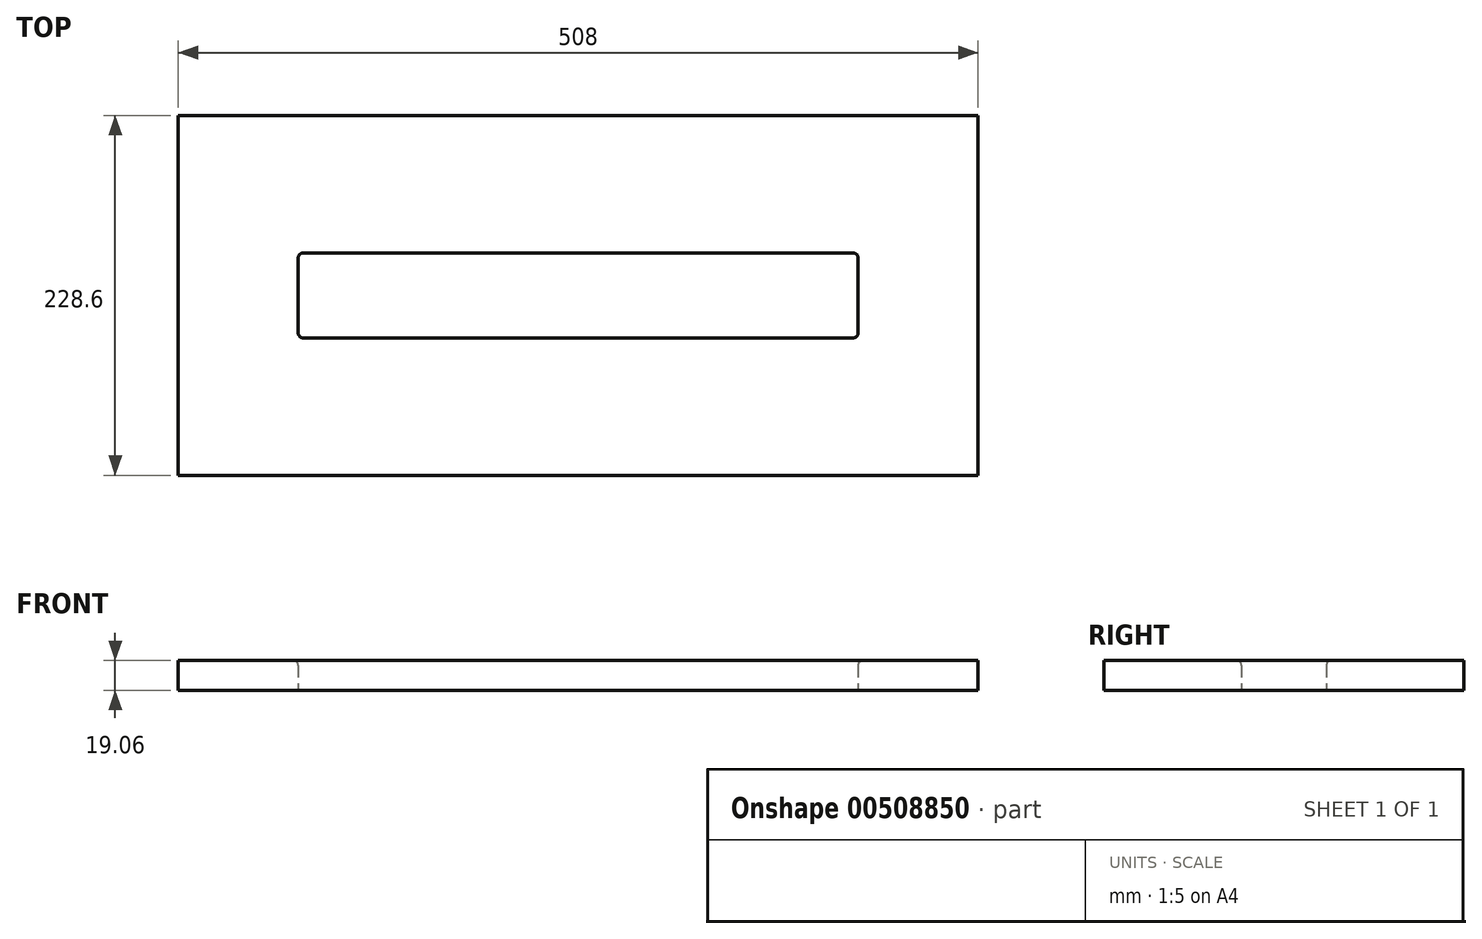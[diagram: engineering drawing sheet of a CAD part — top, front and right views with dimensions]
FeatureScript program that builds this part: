
annotation { "Feature Type Name" : "Feature", "Feature Type Description" : "" }
export const myFeature = defineFeature(function(context is Context, id is Id, definition is map)
    precondition{}
    {
        {
            var Q0;
            Q0=qCreatedBy(makeId("Top.planeOp"),FACE);
            var sketch = newSketch(context, id + "F0", { "sketchPlane" : qUnion([Q0])});
            skLineSegment(sketch, "E0.bottom", {"start": v(254, -114.3) * mm, "end": v(-254, -114.3) * mm});
            skLineSegment(sketch, "E0.top", {"start": v(254, 114.3) * mm, "end": v(-254, 114.3) * mm});
            skLineSegment(sketch, "E0.left", {"start": v(254, -114.3) * mm, "end": v(254, 114.3) * mm});
            skLineSegment(sketch, "E0.right", {"start": v(-254, -114.3) * mm, "end": v(-254, 114.3) * mm});
            skPoint(sketch, "E0.middle", {"position": v(0, 0) * mm});
            skLineSegment(sketch, "E1.bottom", {"start": v(177.8, -26.99) * mm, "end": v(-177.8, -26.99) * mm});
            skLineSegment(sketch, "E1.top", {"start": v(177.8, 26.99) * mm, "end": v(-177.8, 26.99) * mm});
            skLineSegment(sketch, "E1.left", {"start": v(177.8, -26.99) * mm, "end": v(177.8, 26.99) * mm});
            skLineSegment(sketch, "E1.right", {"start": v(-177.8, -26.99) * mm, "end": v(-177.8, 26.99) * mm});
            skSolve(sketch);
        }
        {
            var Q0;
            Q0=makeQuery(id+"F0.imprint","IMPRINT",FACE,{"disambiguationData":[TD([[makeQuery(id+"F0.imprint","IMPRINT",EDGE,{"derivedFrom":sQuery(id+"F0.wireOp",EDGE,"E0.bottom")}),-1.0]])]});
            extrude(context, id + "F1", {"entities" : qUnion([Q0]), "endBound" : BoundingType.SYMMETRIC, "depth" : 19.05 * mm});
        }
        {
            var Q0;
            Q0=makeQuery(id+"F1.opExtrude","CAP_EDGE",EDGE,{"disambiguationData":[OSD([sQuery(id+"F0.wireOp",EDGE,"E1.right")])],"isStart":false});
            var Q1;
            Q1=makeQuery(id+"F1.opExtrude","CAP_EDGE",EDGE,{"disambiguationData":[OSD([sQuery(id+"F0.wireOp",EDGE,"E1.top")])],"isStart":false});
            var Q2;
            Q2=makeQuery(id+"F1.opExtrude","CAP_EDGE",EDGE,{"disambiguationData":[OSD([sQuery(id+"F0.wireOp",EDGE,"E1.bottom")])],"isStart":false});
            var Q3;
            Q3=makeQuery(id+"F1.opExtrude","CAP_EDGE",EDGE,{"disambiguationData":[OSD([sQuery(id+"F0.wireOp",EDGE,"E1.left")])],"isStart":false});
            var Q4;
            Q4=makeQuery(id+"F1.opExtrude","SWEPT_EDGE",EDGE,{"disambiguationData":[OSD([sQuery(id+"F0.wireOp",EDGE,"E1.top"),sQuery(id+"F0.wireOp",EDGE,"E1.left")])]});
            var Q5;
            Q5=makeQuery(id+"F1.opExtrude","SWEPT_EDGE",EDGE,{"disambiguationData":[OSD([sQuery(id+"F0.wireOp",EDGE,"E1.top"),sQuery(id+"F0.wireOp",EDGE,"E1.right")])]});
            var Q6;
            Q6=makeQuery(id+"F1.opExtrude","SWEPT_EDGE",EDGE,{"disambiguationData":[OSD([sQuery(id+"F0.wireOp",EDGE,"E1.bottom"),sQuery(id+"F0.wireOp",EDGE,"E1.right")])]});
            var Q7;
            Q7=makeQuery(id+"F1.opExtrude","SWEPT_EDGE",EDGE,{"disambiguationData":[OSD([sQuery(id+"F0.wireOp",EDGE,"E1.bottom"),sQuery(id+"F0.wireOp",EDGE,"E1.left")])]});
            fillet(context, id + "F2", {"entities" : qUnion([Q0, Q1, Q2, Q3, Q4, Q5, Q6, Q7]), "radius" : 3.17 * mm, "tangentPropagation" : true, "allowEdgeOverflow" : false});
        }
    });
